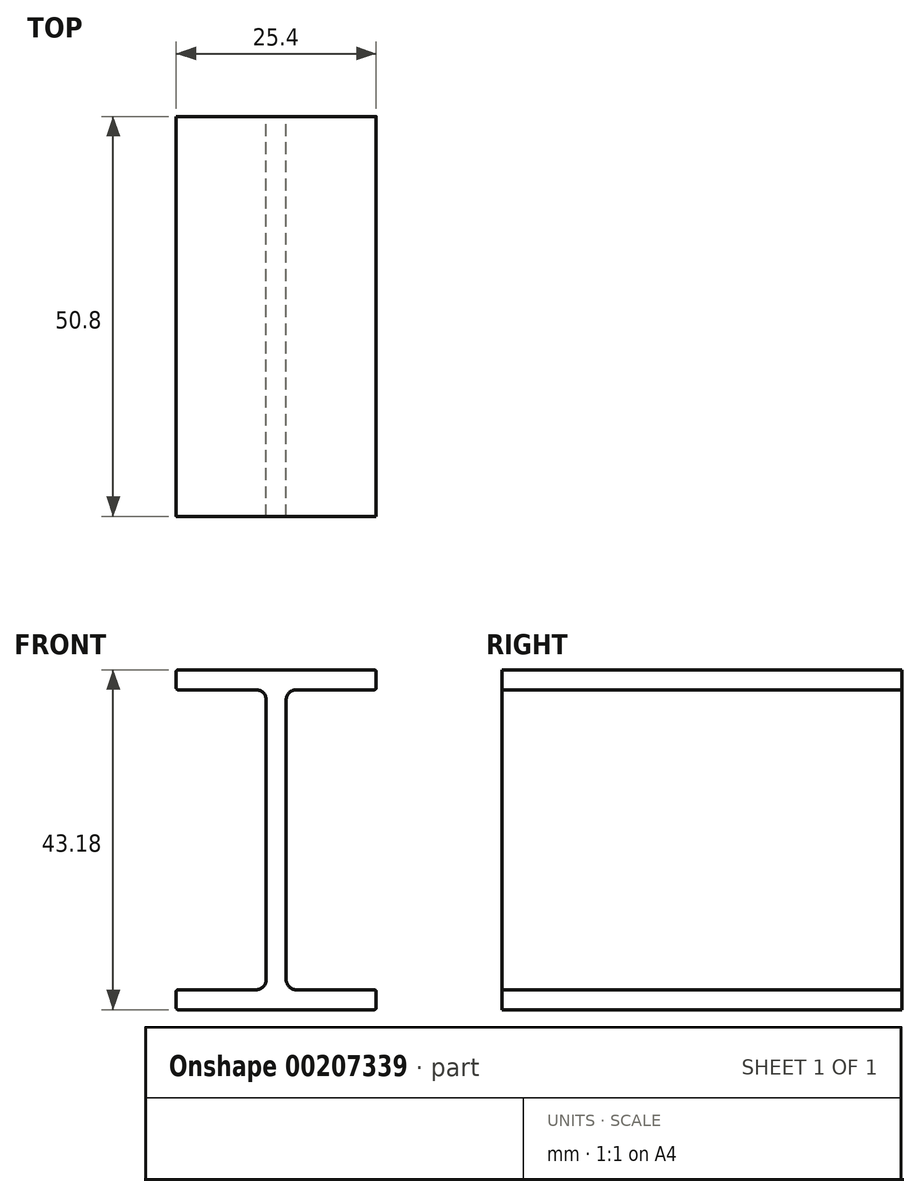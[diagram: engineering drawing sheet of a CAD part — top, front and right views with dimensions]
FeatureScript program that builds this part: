
annotation { "Feature Type Name" : "Feature", "Feature Type Description" : "" }
export const myFeature = defineFeature(function(context is Context, id is Id, definition is map)
    precondition{}
    {
        {
            var Q0;
            Q0=qCreatedBy(makeId("Front.planeOp"),FACE);
            var sketch = newSketch(context, id + "F0", { "sketchPlane" : qUnion([Q0])});
            skLineSegment(sketch, "E0", {"start": v(0, 19.05) * mm, "end": v(0, -19.05) * mm, "construction": true});
            skLineSegment(sketch, "E1", {"start": v(-12.45, 19.05) * mm, "end": v(-2.54, 19.05) * mm});
            skLineSegment(sketch, "E2", {"start": v(-12.45, -19.05) * mm, "end": v(-2.54, -19.05) * mm});
            skLineSegment(sketch, "E3.0", {"start": v(-12.45, -21.59) * mm, "end": v(12.45, -21.59) * mm});
            skLineSegment(sketch, "E4.0", {"start": v(-12.45, 21.6) * mm, "end": v(12.45, 21.6) * mm});
            skLineSegment(sketch, "E5.0", {"start": v(-1.27, 17.78) * mm, "end": v(-1.27, -17.78) * mm});
            skLineSegment(sketch, "E6.0", {"start": v(1.27, 17.78) * mm, "end": v(1.27, -17.78) * mm});
            skLineSegment(sketch, "E7", {"start": v(-12.7, -21.34) * mm, "end": v(-12.7, -19.3) * mm});
            skLineSegment(sketch, "E8", {"start": v(12.7, -19.3) * mm, "end": v(12.7, -21.34) * mm});
            skLineSegment(sketch, "E9", {"start": v(12.7, 19.3) * mm, "end": v(12.7, 21.34) * mm});
            skLineSegment(sketch, "E10", {"start": v(-12.7, 21.34) * mm, "end": v(-12.7, 19.3) * mm});
            skLineSegment(sketch, "E11.trimOffspring", {"start": v(2.54, 19.05) * mm, "end": v(12.45, 19.05) * mm});
            skLineSegment(sketch, "E12.trimOffspring", {"start": v(2.54, -19.05) * mm, "end": v(12.45, -19.05) * mm});
            skPoint(sketch, "E13.visualSharp", {"position": v(-1.27, 19.05) * mm});
            skArc(sketch, "E13.filletArc", {"start": v(-1.27, 17.78) * mm, "mid": v(-1.64, 18.68) * mm, "end": v(-2.54, 19.05) * mm});
            skPoint(sketch, "E14.visualSharp", {"position": v(1.27, 19.05) * mm});
            skArc(sketch, "E14.filletArc", {"start": v(2.54, 19.05) * mm, "mid": v(1.64, 18.68) * mm, "end": v(1.27, 17.78) * mm});
            skPoint(sketch, "E15.visualSharp", {"position": v(-1.27, -19.05) * mm});
            skArc(sketch, "E15.filletArc", {"start": v(-2.54, -19.05) * mm, "mid": v(-1.64, -18.68) * mm, "end": v(-1.27, -17.78) * mm});
            skPoint(sketch, "E16.visualSharp", {"position": v(1.27, -19.05) * mm});
            skArc(sketch, "E16.filletArc", {"start": v(1.27, -17.78) * mm, "mid": v(1.64, -18.68) * mm, "end": v(2.54, -19.05) * mm});
            skPoint(sketch, "E17.visualSharp", {"position": v(-12.7, -19.05) * mm});
            skArc(sketch, "E17.filletArc", {"start": v(-12.45, -19.05) * mm, "mid": v(-12.63, -19.12) * mm, "end": v(-12.7, -19.3) * mm});
            skPoint(sketch, "E18.visualSharp", {"position": v(-12.7, -21.59) * mm});
            skArc(sketch, "E18.filletArc", {"start": v(-12.7, -21.34) * mm, "mid": v(-12.63, -21.52) * mm, "end": v(-12.45, -21.59) * mm});
            skPoint(sketch, "E19.visualSharp", {"position": v(12.7, -21.59) * mm});
            skArc(sketch, "E19.filletArc", {"start": v(12.45, -21.59) * mm, "mid": v(12.63, -21.52) * mm, "end": v(12.7, -21.34) * mm});
            skPoint(sketch, "E20.visualSharp", {"position": v(12.7, -19.05) * mm});
            skArc(sketch, "E20.filletArc", {"start": v(12.7, -19.3) * mm, "mid": v(12.63, -19.12) * mm, "end": v(12.45, -19.05) * mm});
            skPoint(sketch, "E21.visualSharp", {"position": v(12.7, 19.05) * mm});
            skArc(sketch, "E21.filletArc", {"start": v(12.45, 19.05) * mm, "mid": v(12.63, 19.12) * mm, "end": v(12.7, 19.3) * mm});
            skPoint(sketch, "E22.visualSharp", {"position": v(12.7, 21.6) * mm});
            skArc(sketch, "E22.filletArc", {"start": v(12.7, 21.34) * mm, "mid": v(12.63, 21.52) * mm, "end": v(12.45, 21.6) * mm});
            skPoint(sketch, "E23.visualSharp", {"position": v(-12.7, 21.6) * mm});
            skArc(sketch, "E23.filletArc", {"start": v(-12.45, 21.6) * mm, "mid": v(-12.63, 21.52) * mm, "end": v(-12.7, 21.34) * mm});
            skPoint(sketch, "E24.visualSharp", {"position": v(-12.7, 19.05) * mm});
            skArc(sketch, "E24.filletArc", {"start": v(-12.7, 19.3) * mm, "mid": v(-12.63, 19.12) * mm, "end": v(-12.45, 19.05) * mm});
            skSolve(sketch);
        }
        {
            var Q0;
            Q0=makeQuery(id+"F0.imprint","IMPRINT",FACE,{"disambiguationData":[TD([[makeQuery(id+"F0.imprint","IMPRINT",EDGE,{"derivedFrom":sQuery(id+"F0.wireOp",EDGE,"E1")}),1.0]])]});
            extrude(context, id + "F1", {"entities" : qUnion([Q0]), "depth" : 50.8 * mm});
        }
    });
